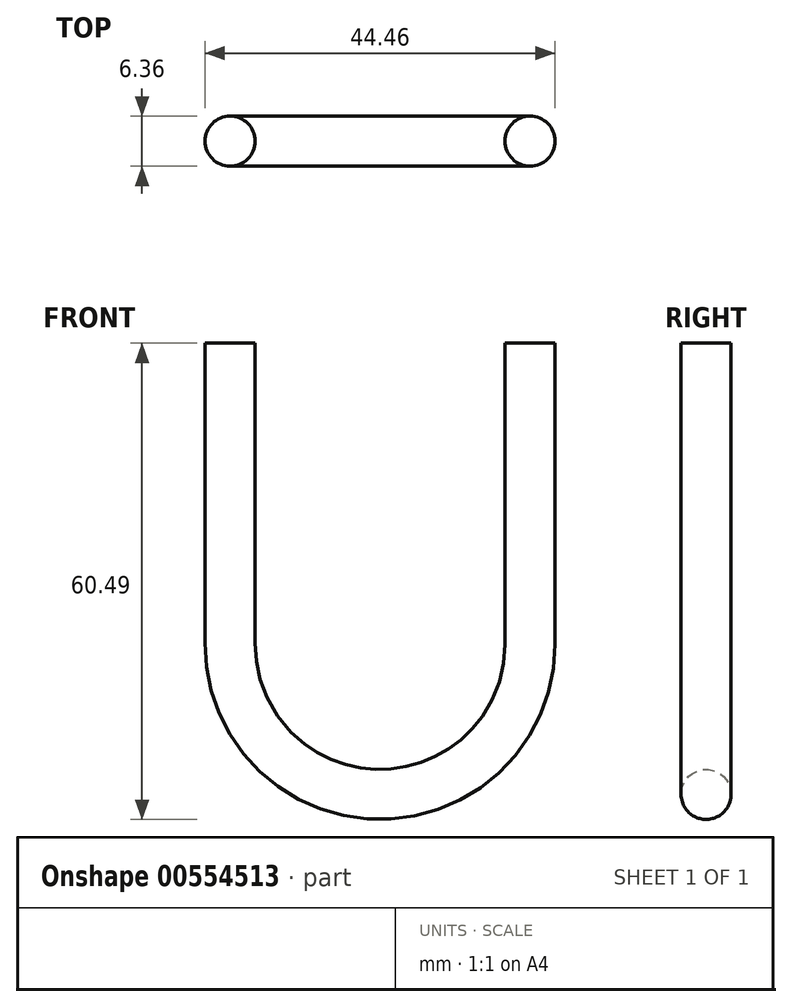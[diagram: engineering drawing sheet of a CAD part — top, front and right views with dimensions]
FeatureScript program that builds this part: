
annotation { "Feature Type Name" : "Feature", "Feature Type Description" : "" }
export const myFeature = defineFeature(function(context is Context, id is Id, definition is map)
    precondition{}
    {
        {
            var Q0;
            Q0=qCreatedBy(makeId("Front.planeOp"),FACE);
            var sketch = newSketch(context, id + "F0", { "sketchPlane" : qUnion([Q0])});
            skLineSegment(sketch, "E0", {"start": v(0, 0) * mm, "end": v(0, -38.26) * mm});
            skArc(sketch, "E1", {"start": v(0, -38.26) * mm, "mid": v(-19.13, -57.31) * mm, "end": v(-38.1, -38.1) * mm});
            skLineSegment(sketch, "E2", {"start": v(-38.1, -38.1) * mm, "end": v(-38.1, 0) * mm});
            skSolve(sketch);
        }
        {
            var Q0;
            Q0=qCreatedBy(makeId("Top.planeOp"),FACE);
            var sketch = newSketch(context, id + "F1", { "sketchPlane" : qUnion([Q0])});
            skCircle(sketch, "E3", {"center": v(0, 0) * mm, "radius": 3.18 * mm});
            skSolve(sketch);
        }
        {
            var Q0;
            Q0=makeQuery(id+"F1.imprint","IMPRINT",FACE,{"disambiguationData":[TD([[makeQuery(id+"F1.imprint","IMPRINT",EDGE,{"derivedFrom":sQuery(id+"F1.wireOp",EDGE,"E3")}),1.0]])]});
            var Q1;
            Q1=sQuery(id+"F0.wireOp",EDGE,"E0");
            var Q2;
            Q2=sQuery(id+"F0.wireOp",EDGE,"E1");
            var Q3;
            Q3=sQuery(id+"F0.wireOp",EDGE,"E2");
            sweep(context, id + "F2", {"profiles" : qUnion([Q0]), "path" : qUnion([Q1, Q2, Q3])});
        }
    });
